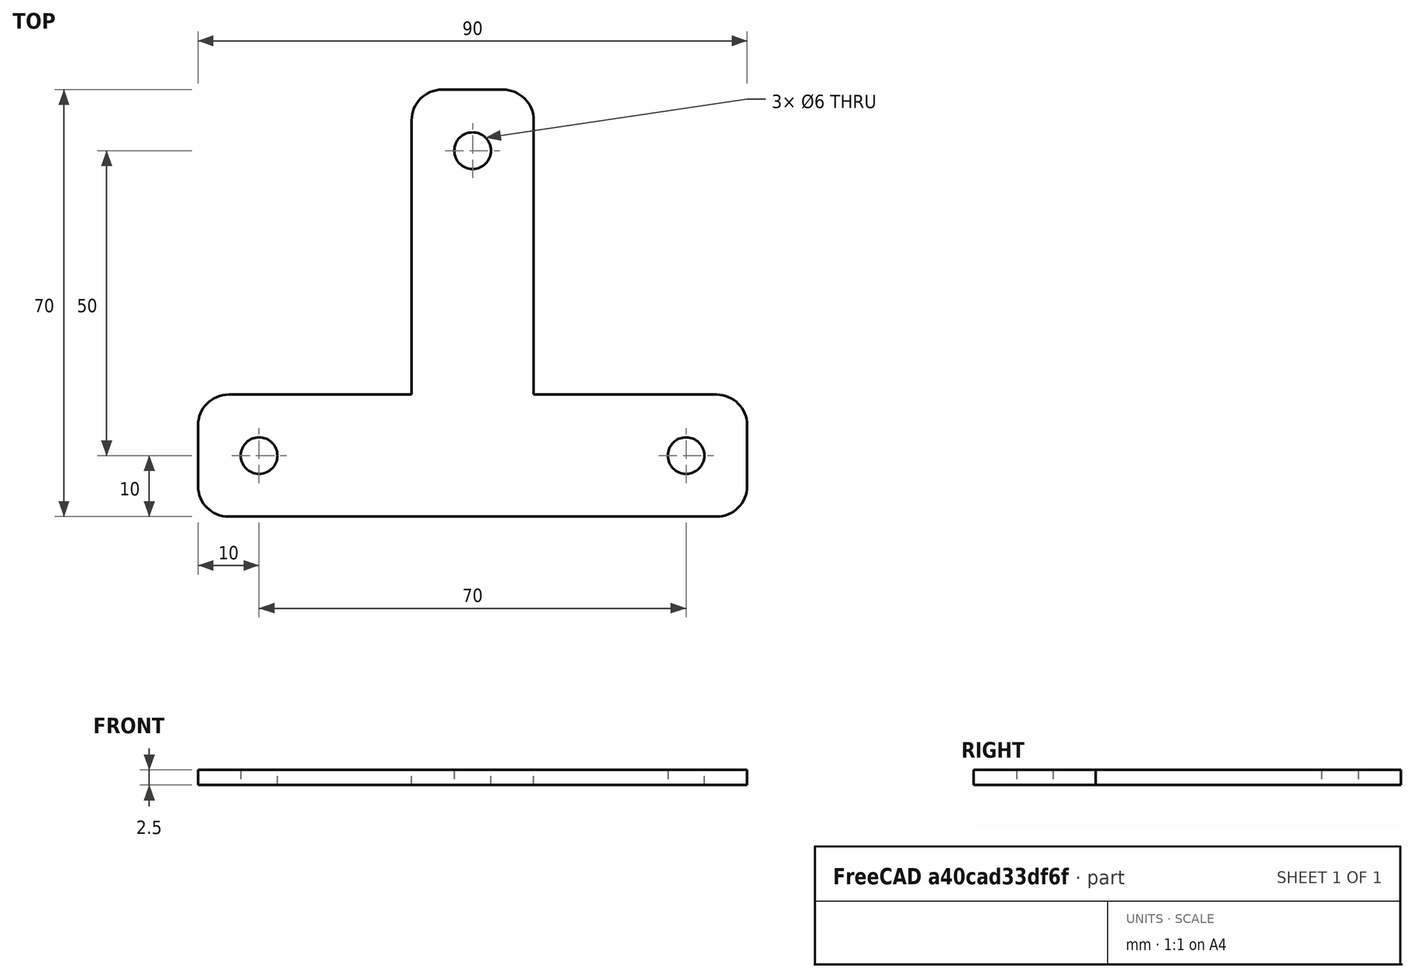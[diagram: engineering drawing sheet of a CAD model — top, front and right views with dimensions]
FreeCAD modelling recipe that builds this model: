
FCSTD DOCUMENT  (FreeCAD 0.19R24276 (Git))
Label: misc_lateral_support
License: All rights reserved
LicenseURL: http://en.wikipedia.org/wiki/All_rights_reserved
objects: Sketcher::SketchObject×1, PartDesign::Pad×1, PartDesign::Body×1
note: 4 computed .brp shape members not serialized (recipe doc carries the construction recipe); baked Part::Feature solids carry a one-line shape summary decoded from their .brp

FEATURE [Sketcher::SketchObject] Sketch
  FullyConstrained = true
  MapMode = 5
  Support = -> [XY_Plane]
  sketch-geometry (17):
    g0: LineSegment StartX=-45 StartY=5 StartZ=0 EndX=-45 EndY=-5 EndZ=0
    g1: LineSegment StartX=-40 StartY=-10 StartZ=0 EndX=40 EndY=-10 EndZ=0
    g2: LineSegment StartX=45 StartY=-5 StartZ=0 EndX=45 EndY=5 EndZ=0
    g3: LineSegment StartX=40 StartY=10 StartZ=0 EndX=10 EndY=10 EndZ=0
    g4: LineSegment StartX=10 StartY=10 StartZ=0 EndX=10 EndY=55 EndZ=0
    g5: LineSegment StartX=5 StartY=60 StartZ=0 EndX=-5 EndY=60 EndZ=0
    g6: LineSegment StartX=-10 StartY=55 StartZ=0 EndX=-10 EndY=10 EndZ=0
    g7: LineSegment StartX=-10 StartY=10 StartZ=0 EndX=-40 EndY=10 EndZ=0
    g8: ArcOfCircle CenterX=-40 CenterY=5 CenterZ=0 NormalX=0 NormalY=0 NormalZ=1 AngleXU=0 Radius=5 StartAngle=1.5708 EndAngle=3.14159
    g9: ArcOfCircle CenterX=-40 CenterY=-5 CenterZ=0 NormalX=0 NormalY=0 NormalZ=1 AngleXU=0 Radius=5 StartAngle=3.14159 EndAngle=4.71239
    g10: ArcOfCircle CenterX=40 CenterY=-5 CenterZ=0 NormalX=0 NormalY=0 NormalZ=1 AngleXU=0 Radius=5 StartAngle=4.71239 EndAngle=6.28319
    g11: ArcOfCircle CenterX=40 CenterY=5 CenterZ=0 NormalX=0 NormalY=0 NormalZ=1 AngleXU=0 Radius=5 StartAngle=0 EndAngle=1.5708
    g12: ArcOfCircle CenterX=-5 CenterY=55 CenterZ=0 NormalX=0 NormalY=0 NormalZ=1 AngleXU=0 Radius=5 StartAngle=1.5708 EndAngle=3.14159
    g13: ArcOfCircle CenterX=5 CenterY=55 CenterZ=0 NormalX=0 NormalY=0 NormalZ=1 AngleXU=0 Radius=5 StartAngle=2e-16 EndAngle=1.5708
    g14: Circle CenterX=-35 CenterY=0 CenterZ=0 NormalX=0 NormalY=0 NormalZ=1 AngleXU=0 Radius=3
    g15: Circle CenterX=35 CenterY=0 CenterZ=0 NormalX=0 NormalY=0 NormalZ=1 AngleXU=0 Radius=3
    g16: Circle CenterX=0 CenterY=50 CenterZ=0 NormalX=0 NormalY=0 NormalZ=1 AngleXU=0 Radius=3
  constraints (45):
    c: Vertical(g0)
    c: Horizontal(g1)
    c: Vertical(g2)
    c: Horizontal(g3)
    c: Coincident(g3,g4)
    c: Vertical(g4)
    c: Horizontal(g5)
    c: Vertical(g6)
    c: Coincident(g6,g7)
    c: Horizontal(g7)
    c: Tangent(g0,g8) = -1.5708
    c: Tangent(g7,g8) = -1.5708
    c: Tangent(g0,g9) = -1.5708
    c: Tangent(g1,g9) = -1.5708
    c: Tangent(g1,g10) = -1.5708
    c: Tangent(g2,g10) = -1.5708
    c: Tangent(g2,g11) = -1.5708
    c: Tangent(g3,g11) = -1.5708
    c: Tangent(g5,g12) = -1.5708
    c: Tangent(g6,g12) = -1.5708
    c: Tangent(g4,g13) = -1.5708
    c: Tangent(g5,g13) = -1.5708
    c: Equal(g12,g13)
    c: Equal(g13,g8)
    c: Equal(g8,g9)
    c: Equal(g9,g10)
    c: Equal(g10,g11)
    c: Equal(g0,g5)
    c: Equal(g5,g2)
    c: Equal(g7,g3)
    c: Diameter(g8) = 10
    c: DistanceY(g1,g7) = 20
    c: DistanceY(g-1,g3) = 10
    c: DistanceX(g-1,g3) = 10
    c: PointOnObject(g14,g-1)
    c: PointOnObject(g15,g-1)
    c: PointOnObject(g16,g-2)
    c: Equal(g14,g16)
    c: Equal(g16,g15)
    c: DistanceX(g0,g14) = 10
    c: DistanceX(g15,g2) = 10
    c: Diameter(g14) = 6
    c: DistanceY(g16,g5) = 10
    c: DistanceY(g1,g5) = 70
    c: DistanceX(g1,g1) = 80
FEATURE [PartDesign::Pad] Pad
  Direction = (1,1,1)
  Length = 2.5
  Length2 = 100
  Profile = -> Sketch
  Type = 0
FEATURE [PartDesign::Body] Body
  Group = -> [Sketch,Pad]
  Origin = -> Origin
  Tip = -> Pad
